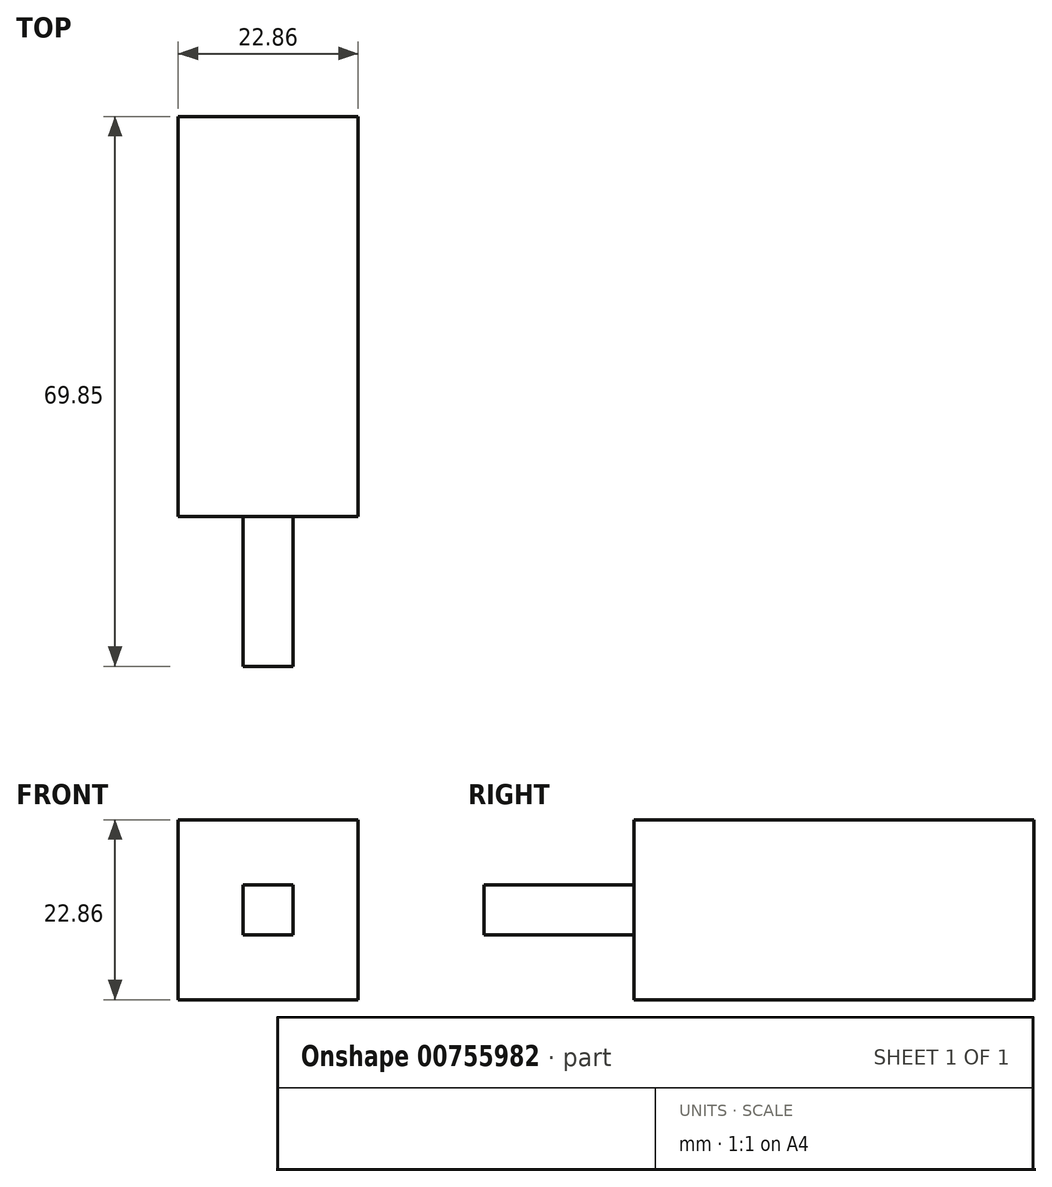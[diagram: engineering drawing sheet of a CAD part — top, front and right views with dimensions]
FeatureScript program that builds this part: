
annotation { "Feature Type Name" : "Feature", "Feature Type Description" : "" }
export const myFeature = defineFeature(function(context is Context, id is Id, definition is map)
    precondition{}
    {
        {
            var Q0;
            Q0=qCreatedBy(makeId("Top.planeOp"),FACE);
            var sketch = newSketch(context, id + "F0", { "sketchPlane" : qUnion([Q0])});
            skLineSegment(sketch, "E0.bottom", {"start": v(0, 0) * mm, "end": v(22.86, 0) * mm});
            skLineSegment(sketch, "E0.top", {"start": v(0, 50.8) * mm, "end": v(22.86, 50.8) * mm});
            skLineSegment(sketch, "E0.left", {"start": v(0, 0) * mm, "end": v(0, 50.8) * mm});
            skLineSegment(sketch, "E0.right", {"start": v(22.86, 0) * mm, "end": v(22.86, 50.8) * mm});
            skSolve(sketch);
        }
        {
            var Q0;
            Q0 = qSketchRegion(id + "F0", true);
            extrude(context, id + "F1", {"entities" : qUnion([Q0]), "depth" : 22.86 * mm, "offsetDistance" : 25.4 * mm});
        }
        {
            var Q0;
            Q0=makeQuery(id+"F1.opExtrude","SWEPT_FACE",FACE,{"disambiguationData":[OSD([sQuery(id+"F0.wireOp",EDGE,"E0.bottom")])]});
            var sketch = newSketch(context, id + "F2", { "sketchPlane" : qUnion([Q0])});
            skLineSegment(sketch, "E1.bottom", {"start": v(8.26, 14.6) * mm, "end": v(14.6, 14.6) * mm});
            skLineSegment(sketch, "E1.top", {"start": v(8.26, 8.25) * mm, "end": v(14.6, 8.25) * mm});
            skLineSegment(sketch, "E1.left", {"start": v(8.26, 14.6) * mm, "end": v(8.26, 8.25) * mm});
            skLineSegment(sketch, "E1.right", {"start": v(14.6, 14.6) * mm, "end": v(14.6, 8.25) * mm});
            skPoint(sketch, "E1.middle", {"position": v(11.43, 11.43) * mm});
            skSolve(sketch);
        }
        {
            var Q0;
            Q0 = qSketchRegion(id + "F2", true);
            extrude(context, id + "F3", {"entities" : qUnion([Q0]), "operationType" : NewBodyOperationType.ADD, "depth" : 19.05 * mm, "offsetDistance" : 25.4 * mm});
        }
    });
